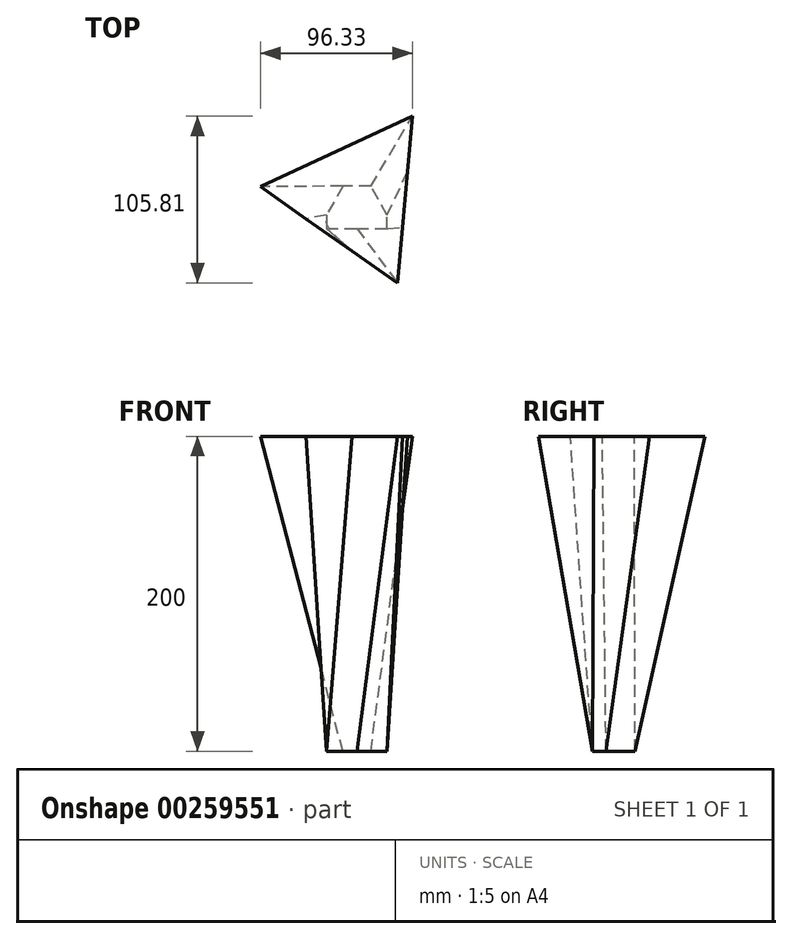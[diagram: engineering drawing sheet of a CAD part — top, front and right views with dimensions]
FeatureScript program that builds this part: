
annotation { "Feature Type Name" : "Feature", "Feature Type Description" : "" }
export const myFeature = defineFeature(function(context is Context, id is Id, definition is map)
    precondition{}
    {
        {
            var Q0;
            Q0=qCreatedBy(makeId("Top.planeOp"),FACE);
            cPlane(context, id + "F0", {"entities" : qUnion([Q0]), "cplaneType" : CPlaneType.OFFSET, "offset" : 100 * mm, "width" : 150 * mm, "height" : 150 * mm});
        }
        {
            var Q0;
            Q0=qCreatedBy(makeId("Top.planeOp"),FACE);
            cPlane(context, id + "F1", {"entities" : qUnion([Q0]), "cplaneType" : CPlaneType.OFFSET, "offset" : 100 * mm, "oppositeDirection" : true, "width" : 150 * mm, "height" : 150 * mm});
        }
        {
            var Q0;
            Q0=qCreatedBy(id+"F1.planeOp",FACE);
            var sketch = newSketch(context, id + "F2", { "sketchPlane" : qUnion([Q0])});
            skLineSegment(sketch, "E0", {"start": v(0, -21.26) * mm, "end": v(19.3, -21.26) * mm});
            skLineSegment(sketch, "E1", {"start": v(19.3, -21.26) * mm, "end": v(19.3, -12.58) * mm});
            skLineSegment(sketch, "E2", {"start": v(19.3, -12.58) * mm, "end": v(8.9, 5.86) * mm});
            skLineSegment(sketch, "E3", {"start": v(8.9, 5.86) * mm, "end": v(-8.9, 5.86) * mm});
            skLineSegment(sketch, "E4", {"start": v(-8.9, 5.86) * mm, "end": v(-19.3, -12.58) * mm});
            skLineSegment(sketch, "E5", {"start": v(-19.3, -12.58) * mm, "end": v(-19.3, -21.26) * mm});
            skLineSegment(sketch, "E6", {"start": v(-19.3, -21.26) * mm, "end": v(0, -21.26) * mm});
            skSolve(sketch);
        }
        {
            var Q0;
            Q0=qCreatedBy(id+"F0.planeOp",FACE);
            var sketch = newSketch(context, id + "F3", { "sketchPlane" : qUnion([Q0])});
            skCircle(sketch, "E7.cCircle", {"center": v(0, 0) * mm, "radius": 30.67 * mm, "construction": true});
            skLineSegment(sketch, "E7.0", {"start": v(35.24, 50.2) * mm, "end": v(25.86, -55.62) * mm});
            skLineSegment(sketch, "E7.1", {"start": v(25.86, -55.62) * mm, "end": v(-61.1, 5.42) * mm});
            skLineSegment(sketch, "E7.2", {"start": v(-61.1, 5.42) * mm, "end": v(35.24, 50.2) * mm});
            skPoint(sketch, "E7.0.midPoint", {"position": v(30.55, -2.7) * mm});
            skSolve(sketch);
        }
        {
            var Q0;
            Q0=makeQuery(id+"F2.imprint","IMPRINT",FACE,{"disambiguationData":[TD([[makeQuery(id+"F2.imprint","IMPRINT",EDGE,{"derivedFrom":sQuery(id+"F2.wireOp",EDGE,"E0")}),1.0]])]});
            var Q1;
            Q1=makeQuery(id+"F3.imprint","IMPRINT",FACE,{"disambiguationData":[TD([[makeQuery(id+"F3.imprint","IMPRINT",EDGE,{"derivedFrom":sQuery(id+"F3.wireOp",EDGE,"E7.0")}),-1.0]])]});
            loft(context, id + "F4", {"sheetProfilesArray" : [{ "sheetProfileEntities" : qUnion([Q0]) }, { "sheetProfileEntities" : qUnion([Q1]) }]});
        }
        {
            var Q0;
            Q0=makeQuery(id+"F4.opLoft","SWEPT_BODY",BODY,{"disambiguationData":[OSD([makeQuery(id+"F2.imprint","IMPRINT",FACE,{"disambiguationData":[TD([[makeQuery(id+"F2.imprint","IMPRINT",EDGE,{"derivedFrom":sQuery(id+"F2.wireOp",EDGE,"E0")}),1.0]])]}),makeQuery(id+"F3.imprint","IMPRINT",FACE,{"disambiguationData":[TD([[makeQuery(id+"F3.imprint","IMPRINT",EDGE,{"derivedFrom":sQuery(id+"F3.wireOp",EDGE,"E7.0")}),-1.0]])]})])]});
            var Q1;
            Q1=makeQuery(id+"F4.opLoft","MID_CAP_VERTEX",VERTEX,{"disambiguationData":[OSD([sQuery(id+"F3.wireOp",EDGE,"E7.1"),sQuery(id+"F3.wireOp",EDGE,"E7.2")])],"capPos":1.0});
            var Q2;
            Q2=makeQuery(id+"F4.opLoft","MID_CAP_VERTEX",VERTEX,{"disambiguationData":[OSD([sQuery(id+"F3.wireOp",EDGE,"E7.0"),sQuery(id+"F3.wireOp",EDGE,"E7.2")])],"capPos":1.0});
            transform(context, id + "F5", {"entities" : qUnion([Q0]), "transformType" : TransformType.TRANSLATION_ENTITY, "oppositeDirectionEntity" : false, "transformLine" : qUnion([Q1, Q2]), "makeCopy" : false});
        }
    });
